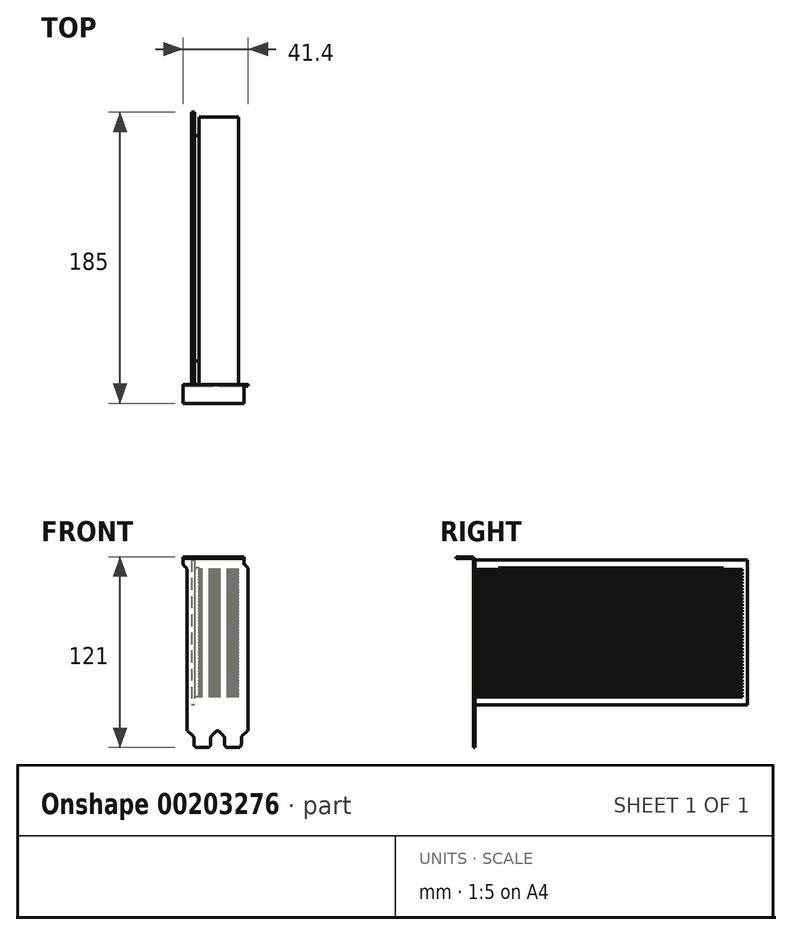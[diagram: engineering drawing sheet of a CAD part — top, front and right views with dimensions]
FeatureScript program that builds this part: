
annotation { "Feature Type Name" : "Feature", "Feature Type Description" : "" }
export const myFeature = defineFeature(function(context is Context, id is Id, definition is map)
    precondition{}
    {
        {
            var Q0;
            Q0=qCreatedBy(makeId("Front.planeOp"),FACE);
            var sketch = newSketch(context, id + "F0", { "sketchPlane" : qUnion([Q0])});
            skLineSegment(sketch, "E0", {"start": v(10.14, 88.78) * mm, "end": v(10.14, -14.22) * mm});
            skLineSegment(sketch, "E1", {"start": v(10.14, -14.22) * mm, "end": v(14.59, -14.22) * mm});
            skLineSegment(sketch, "E2", {"start": v(14.59, -14.22) * mm, "end": v(14.59, -24.82) * mm});
            skLineSegment(sketch, "E3", {"start": v(14.59, -24.82) * mm, "end": v(25.19, -24.82) * mm});
            skLineSegment(sketch, "E4", {"start": v(25.19, -24.82) * mm, "end": v(25.19, -14.22) * mm});
            skLineSegment(sketch, "E5", {"start": v(25.19, -14.22) * mm, "end": v(29.64, -14.22) * mm});
            skLineSegment(sketch, "E6", {"start": v(29.64, -14.22) * mm, "end": v(29.64, 88.78) * mm, "construction": true});
            skLineSegment(sketch, "E7", {"start": v(29.64, -14.22) * mm, "end": v(34.09, -14.22) * mm});
            skLineSegment(sketch, "E8", {"start": v(34.09, -14.22) * mm, "end": v(34.09, -24.82) * mm});
            skLineSegment(sketch, "E9", {"start": v(34.09, -24.82) * mm, "end": v(44.69, -24.82) * mm});
            skLineSegment(sketch, "E10", {"start": v(44.69, -24.82) * mm, "end": v(44.69, -14.22) * mm});
            skLineSegment(sketch, "E11", {"start": v(44.69, -14.22) * mm, "end": v(49.14, -14.22) * mm});
            skLineSegment(sketch, "E12", {"start": v(49.14, -14.22) * mm, "end": v(49.14, 88.78) * mm});
            skLineSegment(sketch, "E13", {"start": v(10.14, 88.78) * mm, "end": v(7.74, 91.18) * mm});
            skLineSegment(sketch, "E14", {"start": v(7.74, 91.18) * mm, "end": v(7.74, 95.18) * mm});
            skLineSegment(sketch, "E15", {"start": v(7.74, 95.18) * mm, "end": v(7.74, 96.18) * mm});
            skLineSegment(sketch, "E16", {"start": v(7.74, 96.18) * mm, "end": v(46.34, 96.18) * mm});
            skLineSegment(sketch, "E17", {"start": v(46.34, 96.18) * mm, "end": v(46.34, 95.18) * mm});
            skLineSegment(sketch, "E18", {"start": v(46.34, 95.18) * mm, "end": v(46.34, 91.58) * mm});
            skLineSegment(sketch, "E19", {"start": v(46.34, 91.58) * mm, "end": v(49.14, 88.78) * mm});
            skLineSegment(sketch, "E20", {"start": v(7.74, 95.18) * mm, "end": v(46.34, 95.18) * mm});
            skSolve(sketch);
        }
        {
            var Q0;
            Q0=makeQuery(id+"F0.imprint","IMPRINT",FACE,{"disambiguationData":[TD([[makeQuery(id+"F0.imprint","IMPRINT",EDGE,{"derivedFrom":sQuery(id+"F0.wireOp",EDGE,"E0")}),1.0]])]});
            extrude(context, id + "F1", {"entities" : qUnion([Q0]), "depth" : 1 * mm});
        }
        {
            var Q0;
            Q0=makeQuery(id+"F1.opExtrude","SWEPT_EDGE",EDGE,{"disambiguationData":[OSD([sQuery(id+"F0.wireOp",EDGE,"E1"),sQuery(id+"F0.wireOp",EDGE,"E2")])]});
            var Q1;
            Q1=makeQuery(id+"F1.opExtrude","SWEPT_EDGE",EDGE,{"disambiguationData":[OSD([sQuery(id+"F0.wireOp",EDGE,"E4"),sQuery(id+"F0.wireOp",EDGE,"E5")])]});
            var Q2;
            Q2=makeQuery(id+"F1.opExtrude","SWEPT_EDGE",EDGE,{"disambiguationData":[OSD([sQuery(id+"F0.wireOp",EDGE,"E7"),sQuery(id+"F0.wireOp",EDGE,"E8")])]});
            var Q3;
            Q3=makeQuery(id+"F1.opExtrude","SWEPT_EDGE",EDGE,{"disambiguationData":[OSD([sQuery(id+"F0.wireOp",EDGE,"E10"),sQuery(id+"F0.wireOp",EDGE,"E11")])]});
            chamfer(context, id + "F2", {"entities" : qUnion([Q0, Q1, Q2, Q3]), "width" : 4 * mm, "tangentPropagation" : true});
        }
        {
            var Q0;
            Q0=makeQuery(id+"F0.imprint","IMPRINT",FACE,{"disambiguationData":[TD([[makeQuery(id+"F0.imprint","IMPRINT",EDGE,{"derivedFrom":sQuery(id+"F0.wireOp",EDGE,"E15")}),-1.0]])]});
            extrude(context, id + "F3", {"entities" : qUnion([Q0]), "operationType" : NewBodyOperationType.ADD, "depth" : 12 * mm});
        }
        {
            var Q0;
            Q0=makeQuery(id+"F3.opExtrude","CAP_EDGE",EDGE,{"disambiguationData":[OSD([sQuery(id+"F0.wireOp",EDGE,"E16")])],"isStart":true});
            var Q1;
            Q1=makeQuery(id+"F1.opExtrude","SWEPT_EDGE",EDGE,{"disambiguationData":[OSD([sQuery(id+"F0.wireOp",EDGE,"E13"),sQuery(id+"F0.wireOp",EDGE,"E14")])]});
            var Q2;
            Q2=makeQuery(id+"F1.opExtrude","SWEPT_EDGE",EDGE,{"disambiguationData":[OSD([sQuery(id+"F0.wireOp",EDGE,"E12"),sQuery(id+"F0.wireOp",EDGE,"E19")])]});
            var Q3;
            Q3=makeQuery(id+"F1.opExtrude","SWEPT_EDGE",EDGE,{"disambiguationData":[OSD([sQuery(id+"F0.wireOp",EDGE,"E18"),sQuery(id+"F0.wireOp",EDGE,"E19")])]});
            var Q4;
            Q4=makeQuery(id+"F1.opExtrude","SWEPT_EDGE",EDGE,{"disambiguationData":[OSD([sQuery(id+"F0.wireOp",EDGE,"E0"),sQuery(id+"F0.wireOp",EDGE,"E13")])]});
            var Q5;
            Q5=makeQuery(id+"F2.opChamfer","BLEND_EDGE",EDGE,{"blendedFrom":[makeQuery(id+"F1.opExtrude","SWEPT_EDGE",EDGE,{"disambiguationData":[OSD([sQuery(id+"F0.wireOp",EDGE,"E1"),sQuery(id+"F0.wireOp",EDGE,"E2")])]}),makeQuery(id+"F1.opExtrude","SWEPT_FACE",FACE,{"disambiguationData":[OSD([sQuery(id+"F0.wireOp",EDGE,"E0")])]})],"blendedInto":[makeQuery(id+"F1.opExtrude","SWEPT_FACE",FACE,{"disambiguationData":[OSD([sQuery(id+"F0.wireOp",EDGE,"E0")])]})]});
            var Q6;
            {var subQ0=sQuery(id+"F0.wireOp",EDGE,"E2");Q6=makeQuery(id+"F2.opChamfer","BLEND_EDGE",EDGE,{"blendedFrom":[makeQuery(id+"F1.opExtrude","SWEPT_EDGE",EDGE,{"disambiguationData":[OSD([sQuery(id+"F0.wireOp",EDGE,"E1"),subQ0])]}),makeQuery(id+"F1.opExtrude","SWEPT_FACE",FACE,{"disambiguationData":[OSD([subQ0])]})],"blendedInto":[makeQuery(id+"F1.opExtrude","SWEPT_FACE",FACE,{"disambiguationData":[OSD([subQ0])]})]});}
            var Q7;
            Q7=makeQuery(id+"F1.opExtrude","SWEPT_EDGE",EDGE,{"disambiguationData":[OSD([sQuery(id+"F0.wireOp",EDGE,"E2"),sQuery(id+"F0.wireOp",EDGE,"E3")])]});
            var Q8;
            Q8=makeQuery(id+"F1.opExtrude","SWEPT_EDGE",EDGE,{"disambiguationData":[OSD([sQuery(id+"F0.wireOp",EDGE,"E3"),sQuery(id+"F0.wireOp",EDGE,"E4")])]});
            var Q9;
            {var subQ0=sQuery(id+"F0.wireOp",EDGE,"E4");Q9=makeQuery(id+"F2.opChamfer","BLEND_EDGE",EDGE,{"blendedFrom":[makeQuery(id+"F1.opExtrude","SWEPT_EDGE",EDGE,{"disambiguationData":[OSD([subQ0,sQuery(id+"F0.wireOp",EDGE,"E5")])]}),makeQuery(id+"F1.opExtrude","SWEPT_FACE",FACE,{"disambiguationData":[OSD([subQ0])]})],"blendedInto":[makeQuery(id+"F1.opExtrude","SWEPT_FACE",FACE,{"disambiguationData":[OSD([subQ0])]})]});}
            var Q10;
            {var subQ0=sQuery(id+"F0.wireOp",EDGE,"E5");Q10=makeQuery(id+"F2.opChamfer","BLEND_EDGE",EDGE,{"blendedFrom":[makeQuery(id+"F1.opExtrude","SWEPT_EDGE",EDGE,{"disambiguationData":[OSD([sQuery(id+"F0.wireOp",EDGE,"E4"),subQ0])]}),makeQuery(id+"F1.opExtrude","SWEPT_FACE",FACE,{"disambiguationData":[OSD([subQ0,sQuery(id+"F0.wireOp",EDGE,"E7")])]})],"blendedInto":[makeQuery(id+"F1.opExtrude","SWEPT_FACE",FACE,{"disambiguationData":[OSD([subQ0,sQuery(id+"F0.wireOp",EDGE,"E7")])]})]});}
            var Q11;
            {var subQ0=sQuery(id+"F0.wireOp",EDGE,"E7");Q11=makeQuery(id+"F2.opChamfer","BLEND_EDGE",EDGE,{"blendedFrom":[makeQuery(id+"F1.opExtrude","SWEPT_EDGE",EDGE,{"disambiguationData":[OSD([subQ0,sQuery(id+"F0.wireOp",EDGE,"E8")])]}),makeQuery(id+"F1.opExtrude","SWEPT_FACE",FACE,{"disambiguationData":[OSD([sQuery(id+"F0.wireOp",EDGE,"E5"),subQ0])]})],"blendedInto":[makeQuery(id+"F1.opExtrude","SWEPT_FACE",FACE,{"disambiguationData":[OSD([sQuery(id+"F0.wireOp",EDGE,"E5"),subQ0])]})]});}
            var Q12;
            {var subQ0=sQuery(id+"F0.wireOp",EDGE,"E8");Q12=makeQuery(id+"F2.opChamfer","BLEND_EDGE",EDGE,{"blendedFrom":[makeQuery(id+"F1.opExtrude","SWEPT_EDGE",EDGE,{"disambiguationData":[OSD([sQuery(id+"F0.wireOp",EDGE,"E7"),subQ0])]}),makeQuery(id+"F1.opExtrude","SWEPT_FACE",FACE,{"disambiguationData":[OSD([subQ0])]})],"blendedInto":[makeQuery(id+"F1.opExtrude","SWEPT_FACE",FACE,{"disambiguationData":[OSD([subQ0])]})]});}
            var Q13;
            Q13=makeQuery(id+"F1.opExtrude","SWEPT_EDGE",EDGE,{"disambiguationData":[OSD([sQuery(id+"F0.wireOp",EDGE,"E8"),sQuery(id+"F0.wireOp",EDGE,"E9")])]});
            var Q14;
            Q14=makeQuery(id+"F1.opExtrude","SWEPT_EDGE",EDGE,{"disambiguationData":[OSD([sQuery(id+"F0.wireOp",EDGE,"E9"),sQuery(id+"F0.wireOp",EDGE,"E10")])]});
            var Q15;
            {var subQ0=sQuery(id+"F0.wireOp",EDGE,"E10");Q15=makeQuery(id+"F2.opChamfer","BLEND_EDGE",EDGE,{"blendedFrom":[makeQuery(id+"F1.opExtrude","SWEPT_EDGE",EDGE,{"disambiguationData":[OSD([subQ0,sQuery(id+"F0.wireOp",EDGE,"E11")])]}),makeQuery(id+"F1.opExtrude","SWEPT_FACE",FACE,{"disambiguationData":[OSD([subQ0])]})],"blendedInto":[makeQuery(id+"F1.opExtrude","SWEPT_FACE",FACE,{"disambiguationData":[OSD([subQ0])]})]});}
            var Q16;
            Q16=makeQuery(id+"F2.opChamfer","BLEND_EDGE",EDGE,{"blendedFrom":[makeQuery(id+"F1.opExtrude","SWEPT_EDGE",EDGE,{"disambiguationData":[OSD([sQuery(id+"F0.wireOp",EDGE,"E10"),sQuery(id+"F0.wireOp",EDGE,"E11")])]}),makeQuery(id+"F1.opExtrude","SWEPT_FACE",FACE,{"disambiguationData":[OSD([sQuery(id+"F0.wireOp",EDGE,"E12")])]})],"blendedInto":[makeQuery(id+"F1.opExtrude","SWEPT_FACE",FACE,{"disambiguationData":[OSD([sQuery(id+"F0.wireOp",EDGE,"E12")])]})]});
            fillet(context, id + "F4", {"entities" : qUnion([Q0, Q1, Q2, Q3, Q4, Q5, Q6, Q7, Q8, Q9, Q10, Q11, Q12, Q13, Q14, Q15, Q16]), "radius" : 2 * mm, "tangentPropagation" : true, "allowEdgeOverflow" : false});
        }
        {
            var Q0;
            {var subQ0=sQuery(id+"F0.wireOp",EDGE,"E20");Q0=makeQuery(id+"F3.boolean.opBoolean","MERGE",FACE,{"derivedFrom":[makeQuery(id+"F1.opExtrude","CAP_FACE",FACE,{"disambiguationData":[OSD([sQuery(id+"F0.wireOp",EDGE,"E0"),sQuery(id+"F0.wireOp",EDGE,"E1"),sQuery(id+"F0.wireOp",EDGE,"E2"),sQuery(id+"F0.wireOp",EDGE,"E3"),sQuery(id+"F0.wireOp",EDGE,"E4"),sQuery(id+"F0.wireOp",EDGE,"E5"),sQuery(id+"F0.wireOp",EDGE,"E7"),sQuery(id+"F0.wireOp",EDGE,"E8"),sQuery(id+"F0.wireOp",EDGE,"E9"),sQuery(id+"F0.wireOp",EDGE,"E10"),sQuery(id+"F0.wireOp",EDGE,"E11"),sQuery(id+"F0.wireOp",EDGE,"E12"),sQuery(id+"F0.wireOp",EDGE,"E13"),sQuery(id+"F0.wireOp",EDGE,"E14"),sQuery(id+"F0.wireOp",EDGE,"E18"),sQuery(id+"F0.wireOp",EDGE,"E19"),subQ0])],"isStart":true}),makeQuery(id+"F3.opExtrude","CAP_FACE",FACE,{"disambiguationData":[OSD([sQuery(id+"F0.wireOp",EDGE,"E15"),sQuery(id+"F0.wireOp",EDGE,"E16"),sQuery(id+"F0.wireOp",EDGE,"E17"),subQ0])],"isStart":true})]});}
            var sketch = newSketch(context, id + "F5", { "sketchPlane" : qUnion([Q0])});
            skLineSegment(sketch, "E21.bottom", {"start": v(-14.94, 100.18) * mm, "end": v(-13.14, 100.18) * mm});
            skLineSegment(sketch, "E21.top", {"start": v(-14.94, 2.18) * mm, "end": v(-13.14, 2.18) * mm});
            skLineSegment(sketch, "E21.left", {"start": v(-14.94, 100.18) * mm, "end": v(-14.94, 2.18) * mm});
            skLineSegment(sketch, "E21.right", {"start": v(-13.14, 100.18) * mm, "end": v(-13.14, 2.18) * mm});
            skLineSegment(sketch, "E22", {"start": v(-19.89, -24.82) * mm, "end": v(-2.6, -24.82) * mm, "construction": true});
            skSolve(sketch);
        }
        {
            var Q0;
            {var subQ0=sQuery(id+"F5.wireOp",EDGE,"E21.top");Q0=makeQuery(id+"F5.imprint","IMPRINT",FACE,{"disambiguationData":[TD([[makeQuery(id+"F5.imprint","IMPRINT",EDGE,{"derivedFrom":subQ0}),1.0]])]});}
            extrude(context, id + "F6", {"entities" : qUnion([Q0]), "operationType" : NewBodyOperationType.ADD, "depth" : 173 * mm});
        }
        {
            var Q0;
            Q0=makeQuery(id+"F6.opExtrude","SWEPT_FACE",FACE,{"disambiguationData":[OSD([sQuery(id+"F5.wireOp",EDGE,"E21.left")])]});
            var sketch = newSketch(context, id + "F7", { "sketchPlane" : qUnion([Q0])});
            skLineSegment(sketch, "E23.bottom", {"start": v(15, 89.18) * mm, "end": v(158, 89.18) * mm});
            skLineSegment(sketch, "E23.top", {"start": v(15, 7.18) * mm, "end": v(158, 7.18) * mm});
            skLineSegment(sketch, "E23.left", {"start": v(15, 89.18) * mm, "end": v(15, 7.18) * mm});
            skLineSegment(sketch, "E23.right", {"start": v(158, 89.18) * mm, "end": v(158, 7.18) * mm});
            skSolve(sketch);
        }
        {
            var Q0;
            Q0=makeQuery(id+"F7.imprint","IMPRINT",FACE,{"disambiguationData":[TD([[makeQuery(id+"F7.imprint","IMPRINT",EDGE,{"derivedFrom":sQuery(id+"F7.wireOp",EDGE,"E23.bottom")}),-1.0]])]});
            extrude(context, id + "F8", {"entities" : qUnion([Q0]), "operationType" : NewBodyOperationType.ADD, "depth" : 3 * mm});
        }
        {
            var Q0;
            Q0=makeQuery(id+"F8.opExtrude","CAP_FACE",FACE,{"disambiguationData":[OSD([sQuery(id+"F7.wireOp",EDGE,"E23.bottom"),sQuery(id+"F7.wireOp",EDGE,"E23.top"),sQuery(id+"F7.wireOp",EDGE,"E23.left"),sQuery(id+"F7.wireOp",EDGE,"E23.right")])],"isStart":false});
            var sketch = newSketch(context, id + "F9", { "sketchPlane" : qUnion([Q0])});
            skLineSegment(sketch, "E24.bottom", {"start": v(0, 7.18) * mm, "end": v(170, 7.18) * mm});
            skLineSegment(sketch, "E24.top", {"start": v(0, 8.18) * mm, "end": v(170, 8.18) * mm});
            skLineSegment(sketch, "E24.left", {"start": v(0, 7.18) * mm, "end": v(0, 8.18) * mm});
            skLineSegment(sketch, "E24.right", {"start": v(170, 7.18) * mm, "end": v(170, 8.18) * mm});
            skLineSegment(sketch, "E25.0.1.0", {"start": v(0, 10.18) * mm, "end": v(170, 10.18) * mm});
            skLineSegment(sketch, "E25.0.1.1", {"start": v(0, 9.18) * mm, "end": v(170, 9.18) * mm});
            skLineSegment(sketch, "E25.0.1.2", {"start": v(0, 9.18) * mm, "end": v(0, 10.18) * mm});
            skLineSegment(sketch, "E25.0.1.3", {"start": v(170, 9.18) * mm, "end": v(170, 10.18) * mm});
            skLineSegment(sketch, "E25.0.2.0", {"start": v(0, 12.18) * mm, "end": v(170, 12.18) * mm});
            skLineSegment(sketch, "E25.0.2.1", {"start": v(0, 11.18) * mm, "end": v(170, 11.18) * mm});
            skLineSegment(sketch, "E25.0.2.2", {"start": v(0, 11.18) * mm, "end": v(0, 12.18) * mm});
            skLineSegment(sketch, "E25.0.2.3", {"start": v(170, 11.18) * mm, "end": v(170, 12.18) * mm});
            skLineSegment(sketch, "E25.0.3.0", {"start": v(0, 14.18) * mm, "end": v(170, 14.18) * mm});
            skLineSegment(sketch, "E25.0.3.1", {"start": v(0, 13.18) * mm, "end": v(170, 13.18) * mm});
            skLineSegment(sketch, "E25.0.3.2", {"start": v(0, 13.18) * mm, "end": v(0, 14.18) * mm});
            skLineSegment(sketch, "E25.0.3.3", {"start": v(170, 13.18) * mm, "end": v(170, 14.18) * mm});
            skLineSegment(sketch, "E25.0.4.0", {"start": v(0, 16.18) * mm, "end": v(170, 16.18) * mm});
            skLineSegment(sketch, "E25.0.4.1", {"start": v(0, 15.18) * mm, "end": v(170, 15.18) * mm});
            skLineSegment(sketch, "E25.0.4.2", {"start": v(0, 15.18) * mm, "end": v(0, 16.18) * mm});
            skLineSegment(sketch, "E25.0.4.3", {"start": v(170, 15.18) * mm, "end": v(170, 16.18) * mm});
            skLineSegment(sketch, "E25.0.5.0", {"start": v(0, 18.18) * mm, "end": v(170, 18.18) * mm});
            skLineSegment(sketch, "E25.0.5.1", {"start": v(0, 17.18) * mm, "end": v(170, 17.18) * mm});
            skLineSegment(sketch, "E25.0.5.2", {"start": v(0, 17.18) * mm, "end": v(0, 18.18) * mm});
            skLineSegment(sketch, "E25.0.5.3", {"start": v(170, 17.18) * mm, "end": v(170, 18.18) * mm});
            skLineSegment(sketch, "E25.0.6.0", {"start": v(0, 20.18) * mm, "end": v(170, 20.18) * mm});
            skLineSegment(sketch, "E25.0.6.1", {"start": v(0, 19.18) * mm, "end": v(170, 19.18) * mm});
            skLineSegment(sketch, "E25.0.6.2", {"start": v(0, 19.18) * mm, "end": v(0, 20.18) * mm});
            skLineSegment(sketch, "E25.0.6.3", {"start": v(170, 19.18) * mm, "end": v(170, 20.18) * mm});
            skLineSegment(sketch, "E25.0.7.0", {"start": v(0, 22.18) * mm, "end": v(170, 22.18) * mm});
            skLineSegment(sketch, "E25.0.7.1", {"start": v(0, 21.18) * mm, "end": v(170, 21.18) * mm});
            skLineSegment(sketch, "E25.0.7.2", {"start": v(0, 21.18) * mm, "end": v(0, 22.18) * mm});
            skLineSegment(sketch, "E25.0.7.3", {"start": v(170, 21.18) * mm, "end": v(170, 22.18) * mm});
            skLineSegment(sketch, "E25.0.8.0", {"start": v(0, 24.18) * mm, "end": v(170, 24.18) * mm});
            skLineSegment(sketch, "E25.0.8.1", {"start": v(0, 23.18) * mm, "end": v(170, 23.18) * mm});
            skLineSegment(sketch, "E25.0.8.2", {"start": v(0, 23.18) * mm, "end": v(0, 24.18) * mm});
            skLineSegment(sketch, "E25.0.8.3", {"start": v(170, 23.18) * mm, "end": v(170, 24.18) * mm});
            skLineSegment(sketch, "E25.0.9.0", {"start": v(0, 26.18) * mm, "end": v(170, 26.18) * mm});
            skLineSegment(sketch, "E25.0.9.1", {"start": v(0, 25.18) * mm, "end": v(170, 25.18) * mm});
            skLineSegment(sketch, "E25.0.9.2", {"start": v(0, 25.18) * mm, "end": v(0, 26.18) * mm});
            skLineSegment(sketch, "E25.0.9.3", {"start": v(170, 25.18) * mm, "end": v(170, 26.18) * mm});
            skLineSegment(sketch, "E25.0.10.0", {"start": v(0, 28.18) * mm, "end": v(170, 28.18) * mm});
            skLineSegment(sketch, "E25.0.10.1", {"start": v(0, 27.18) * mm, "end": v(170, 27.18) * mm});
            skLineSegment(sketch, "E25.0.10.2", {"start": v(0, 27.18) * mm, "end": v(0, 28.18) * mm});
            skLineSegment(sketch, "E25.0.10.3", {"start": v(170, 27.18) * mm, "end": v(170, 28.18) * mm});
            skLineSegment(sketch, "E25.0.11.0", {"start": v(0, 30.18) * mm, "end": v(170, 30.18) * mm});
            skLineSegment(sketch, "E25.0.11.1", {"start": v(0, 29.18) * mm, "end": v(170, 29.18) * mm});
            skLineSegment(sketch, "E25.0.11.2", {"start": v(0, 29.18) * mm, "end": v(0, 30.18) * mm});
            skLineSegment(sketch, "E25.0.11.3", {"start": v(170, 29.18) * mm, "end": v(170, 30.18) * mm});
            skLineSegment(sketch, "E25.0.12.0", {"start": v(0, 32.18) * mm, "end": v(170, 32.18) * mm});
            skLineSegment(sketch, "E25.0.12.1", {"start": v(0, 31.18) * mm, "end": v(170, 31.18) * mm});
            skLineSegment(sketch, "E25.0.12.2", {"start": v(0, 31.18) * mm, "end": v(0, 32.18) * mm});
            skLineSegment(sketch, "E25.0.12.3", {"start": v(170, 31.18) * mm, "end": v(170, 32.18) * mm});
            skLineSegment(sketch, "E25.0.13.0", {"start": v(0, 34.18) * mm, "end": v(170, 34.18) * mm});
            skLineSegment(sketch, "E25.0.13.1", {"start": v(0, 33.18) * mm, "end": v(170, 33.18) * mm});
            skLineSegment(sketch, "E25.0.13.2", {"start": v(0, 33.18) * mm, "end": v(0, 34.18) * mm});
            skLineSegment(sketch, "E25.0.13.3", {"start": v(170, 33.18) * mm, "end": v(170, 34.18) * mm});
            skLineSegment(sketch, "E25.0.14.0", {"start": v(0, 36.18) * mm, "end": v(170, 36.18) * mm});
            skLineSegment(sketch, "E25.0.14.1", {"start": v(0, 35.18) * mm, "end": v(170, 35.18) * mm});
            skLineSegment(sketch, "E25.0.14.2", {"start": v(0, 35.18) * mm, "end": v(0, 36.18) * mm});
            skLineSegment(sketch, "E25.0.14.3", {"start": v(170, 35.18) * mm, "end": v(170, 36.18) * mm});
            skLineSegment(sketch, "E25.0.15.0", {"start": v(0, 38.18) * mm, "end": v(170, 38.18) * mm});
            skLineSegment(sketch, "E25.0.15.1", {"start": v(0, 37.18) * mm, "end": v(170, 37.18) * mm});
            skLineSegment(sketch, "E25.0.15.2", {"start": v(0, 37.18) * mm, "end": v(0, 38.18) * mm});
            skLineSegment(sketch, "E25.0.15.3", {"start": v(170, 37.18) * mm, "end": v(170, 38.18) * mm});
            skLineSegment(sketch, "E25.0.16.0", {"start": v(0, 40.18) * mm, "end": v(170, 40.18) * mm});
            skLineSegment(sketch, "E25.0.16.1", {"start": v(0, 39.18) * mm, "end": v(170, 39.18) * mm});
            skLineSegment(sketch, "E25.0.16.2", {"start": v(0, 39.18) * mm, "end": v(0, 40.18) * mm});
            skLineSegment(sketch, "E25.0.16.3", {"start": v(170, 39.18) * mm, "end": v(170, 40.18) * mm});
            skLineSegment(sketch, "E25.0.17.0", {"start": v(0, 42.18) * mm, "end": v(170, 42.18) * mm});
            skLineSegment(sketch, "E25.0.17.1", {"start": v(0, 41.18) * mm, "end": v(170, 41.18) * mm});
            skLineSegment(sketch, "E25.0.17.2", {"start": v(0, 41.18) * mm, "end": v(0, 42.18) * mm});
            skLineSegment(sketch, "E25.0.17.3", {"start": v(170, 41.18) * mm, "end": v(170, 42.18) * mm});
            skLineSegment(sketch, "E25.0.18.0", {"start": v(0, 44.18) * mm, "end": v(170, 44.18) * mm});
            skLineSegment(sketch, "E25.0.18.1", {"start": v(0, 43.18) * mm, "end": v(170, 43.18) * mm});
            skLineSegment(sketch, "E25.0.18.2", {"start": v(0, 43.18) * mm, "end": v(0, 44.18) * mm});
            skLineSegment(sketch, "E25.0.18.3", {"start": v(170, 43.18) * mm, "end": v(170, 44.18) * mm});
            skLineSegment(sketch, "E25.0.19.0", {"start": v(0, 46.18) * mm, "end": v(170, 46.18) * mm});
            skLineSegment(sketch, "E25.0.19.1", {"start": v(0, 45.18) * mm, "end": v(170, 45.18) * mm});
            skLineSegment(sketch, "E25.0.19.2", {"start": v(0, 45.18) * mm, "end": v(0, 46.18) * mm});
            skLineSegment(sketch, "E25.0.19.3", {"start": v(170, 45.18) * mm, "end": v(170, 46.18) * mm});
            skLineSegment(sketch, "E25.0.20.0", {"start": v(0, 48.18) * mm, "end": v(170, 48.18) * mm});
            skLineSegment(sketch, "E25.0.20.1", {"start": v(0, 47.18) * mm, "end": v(170, 47.18) * mm});
            skLineSegment(sketch, "E25.0.20.2", {"start": v(0, 47.18) * mm, "end": v(0, 48.18) * mm});
            skLineSegment(sketch, "E25.0.20.3", {"start": v(170, 47.18) * mm, "end": v(170, 48.18) * mm});
            skLineSegment(sketch, "E25.0.21.0", {"start": v(0, 50.18) * mm, "end": v(170, 50.18) * mm});
            skLineSegment(sketch, "E25.0.21.1", {"start": v(0, 49.18) * mm, "end": v(170, 49.18) * mm});
            skLineSegment(sketch, "E25.0.21.2", {"start": v(0, 49.18) * mm, "end": v(0, 50.18) * mm});
            skLineSegment(sketch, "E25.0.21.3", {"start": v(170, 49.18) * mm, "end": v(170, 50.18) * mm});
            skLineSegment(sketch, "E25.0.22.0", {"start": v(0, 52.18) * mm, "end": v(170, 52.18) * mm});
            skLineSegment(sketch, "E25.0.22.1", {"start": v(0, 51.18) * mm, "end": v(170, 51.18) * mm});
            skLineSegment(sketch, "E25.0.22.2", {"start": v(0, 51.18) * mm, "end": v(0, 52.18) * mm});
            skLineSegment(sketch, "E25.0.22.3", {"start": v(170, 51.18) * mm, "end": v(170, 52.18) * mm});
            skLineSegment(sketch, "E25.0.23.0", {"start": v(0, 54.18) * mm, "end": v(170, 54.18) * mm});
            skLineSegment(sketch, "E25.0.23.1", {"start": v(0, 53.18) * mm, "end": v(170, 53.18) * mm});
            skLineSegment(sketch, "E25.0.23.2", {"start": v(0, 53.18) * mm, "end": v(0, 54.18) * mm});
            skLineSegment(sketch, "E25.0.23.3", {"start": v(170, 53.18) * mm, "end": v(170, 54.18) * mm});
            skLineSegment(sketch, "E25.0.24.0", {"start": v(0, 56.18) * mm, "end": v(170, 56.18) * mm});
            skLineSegment(sketch, "E25.0.24.1", {"start": v(0, 55.18) * mm, "end": v(170, 55.18) * mm});
            skLineSegment(sketch, "E25.0.24.2", {"start": v(0, 55.18) * mm, "end": v(0, 56.18) * mm});
            skLineSegment(sketch, "E25.0.24.3", {"start": v(170, 55.18) * mm, "end": v(170, 56.18) * mm});
            skLineSegment(sketch, "E25.0.25.0", {"start": v(0, 58.18) * mm, "end": v(170, 58.18) * mm});
            skLineSegment(sketch, "E25.0.25.1", {"start": v(0, 57.18) * mm, "end": v(170, 57.18) * mm});
            skLineSegment(sketch, "E25.0.25.2", {"start": v(0, 57.18) * mm, "end": v(0, 58.18) * mm});
            skLineSegment(sketch, "E25.0.25.3", {"start": v(170, 57.18) * mm, "end": v(170, 58.18) * mm});
            skLineSegment(sketch, "E25.0.26.0", {"start": v(0, 60.18) * mm, "end": v(170, 60.18) * mm});
            skLineSegment(sketch, "E25.0.26.1", {"start": v(0, 59.18) * mm, "end": v(170, 59.18) * mm});
            skLineSegment(sketch, "E25.0.26.2", {"start": v(0, 59.18) * mm, "end": v(0, 60.18) * mm});
            skLineSegment(sketch, "E25.0.26.3", {"start": v(170, 59.18) * mm, "end": v(170, 60.18) * mm});
            skLineSegment(sketch, "E25.0.27.0", {"start": v(0, 62.18) * mm, "end": v(170, 62.18) * mm});
            skLineSegment(sketch, "E25.0.27.1", {"start": v(0, 61.18) * mm, "end": v(170, 61.18) * mm});
            skLineSegment(sketch, "E25.0.27.2", {"start": v(0, 61.18) * mm, "end": v(0, 62.18) * mm});
            skLineSegment(sketch, "E25.0.27.3", {"start": v(170, 61.18) * mm, "end": v(170, 62.18) * mm});
            skLineSegment(sketch, "E25.0.28.0", {"start": v(0, 64.18) * mm, "end": v(170, 64.18) * mm});
            skLineSegment(sketch, "E25.0.28.1", {"start": v(0, 63.18) * mm, "end": v(170, 63.18) * mm});
            skLineSegment(sketch, "E25.0.28.2", {"start": v(0, 63.18) * mm, "end": v(0, 64.18) * mm});
            skLineSegment(sketch, "E25.0.28.3", {"start": v(170, 63.18) * mm, "end": v(170, 64.18) * mm});
            skLineSegment(sketch, "E25.0.29.0", {"start": v(0, 66.18) * mm, "end": v(170, 66.18) * mm});
            skLineSegment(sketch, "E25.0.29.1", {"start": v(0, 65.18) * mm, "end": v(170, 65.18) * mm});
            skLineSegment(sketch, "E25.0.29.2", {"start": v(0, 65.18) * mm, "end": v(0, 66.18) * mm});
            skLineSegment(sketch, "E25.0.29.3", {"start": v(170, 65.18) * mm, "end": v(170, 66.18) * mm});
            skLineSegment(sketch, "E25.0.30.0", {"start": v(0, 68.18) * mm, "end": v(170, 68.18) * mm});
            skLineSegment(sketch, "E25.0.30.1", {"start": v(0, 67.18) * mm, "end": v(170, 67.18) * mm});
            skLineSegment(sketch, "E25.0.30.2", {"start": v(0, 67.18) * mm, "end": v(0, 68.18) * mm});
            skLineSegment(sketch, "E25.0.30.3", {"start": v(170, 67.18) * mm, "end": v(170, 68.18) * mm});
            skLineSegment(sketch, "E25.0.31.0", {"start": v(0, 70.18) * mm, "end": v(170, 70.18) * mm});
            skLineSegment(sketch, "E25.0.31.1", {"start": v(0, 69.18) * mm, "end": v(170, 69.18) * mm});
            skLineSegment(sketch, "E25.0.31.2", {"start": v(0, 69.18) * mm, "end": v(0, 70.18) * mm});
            skLineSegment(sketch, "E25.0.31.3", {"start": v(170, 69.18) * mm, "end": v(170, 70.18) * mm});
            skLineSegment(sketch, "E25.0.32.0", {"start": v(0, 72.18) * mm, "end": v(170, 72.18) * mm});
            skLineSegment(sketch, "E25.0.32.1", {"start": v(0, 71.18) * mm, "end": v(170, 71.18) * mm});
            skLineSegment(sketch, "E25.0.32.2", {"start": v(0, 71.18) * mm, "end": v(0, 72.18) * mm});
            skLineSegment(sketch, "E25.0.32.3", {"start": v(170, 71.18) * mm, "end": v(170, 72.18) * mm});
            skLineSegment(sketch, "E25.0.33.0", {"start": v(0, 74.18) * mm, "end": v(170, 74.18) * mm});
            skLineSegment(sketch, "E25.0.33.1", {"start": v(0, 73.18) * mm, "end": v(170, 73.18) * mm});
            skLineSegment(sketch, "E25.0.33.2", {"start": v(0, 73.18) * mm, "end": v(0, 74.18) * mm});
            skLineSegment(sketch, "E25.0.33.3", {"start": v(170, 73.18) * mm, "end": v(170, 74.18) * mm});
            skLineSegment(sketch, "E25.0.34.0", {"start": v(0, 76.18) * mm, "end": v(170, 76.18) * mm});
            skLineSegment(sketch, "E25.0.34.1", {"start": v(0, 75.18) * mm, "end": v(170, 75.18) * mm});
            skLineSegment(sketch, "E25.0.34.2", {"start": v(0, 75.18) * mm, "end": v(0, 76.18) * mm});
            skLineSegment(sketch, "E25.0.34.3", {"start": v(170, 75.18) * mm, "end": v(170, 76.18) * mm});
            skLineSegment(sketch, "E25.0.35.0", {"start": v(0, 78.18) * mm, "end": v(170, 78.18) * mm});
            skLineSegment(sketch, "E25.0.35.1", {"start": v(0, 77.18) * mm, "end": v(170, 77.18) * mm});
            skLineSegment(sketch, "E25.0.35.2", {"start": v(0, 77.18) * mm, "end": v(0, 78.18) * mm});
            skLineSegment(sketch, "E25.0.35.3", {"start": v(170, 77.18) * mm, "end": v(170, 78.18) * mm});
            skLineSegment(sketch, "E25.0.36.0", {"start": v(0, 80.18) * mm, "end": v(170, 80.18) * mm});
            skLineSegment(sketch, "E25.0.36.1", {"start": v(0, 79.18) * mm, "end": v(170, 79.18) * mm});
            skLineSegment(sketch, "E25.0.36.2", {"start": v(0, 79.18) * mm, "end": v(0, 80.18) * mm});
            skLineSegment(sketch, "E25.0.36.3", {"start": v(170, 79.18) * mm, "end": v(170, 80.18) * mm});
            skLineSegment(sketch, "E25.0.37.0", {"start": v(0, 82.18) * mm, "end": v(170, 82.18) * mm});
            skLineSegment(sketch, "E25.0.37.1", {"start": v(0, 81.18) * mm, "end": v(170, 81.18) * mm});
            skLineSegment(sketch, "E25.0.37.2", {"start": v(0, 81.18) * mm, "end": v(0, 82.18) * mm});
            skLineSegment(sketch, "E25.0.37.3", {"start": v(170, 81.18) * mm, "end": v(170, 82.18) * mm});
            skLineSegment(sketch, "E25.0.38.0", {"start": v(0, 84.18) * mm, "end": v(170, 84.18) * mm});
            skLineSegment(sketch, "E25.0.38.1", {"start": v(0, 83.18) * mm, "end": v(170, 83.18) * mm});
            skLineSegment(sketch, "E25.0.38.2", {"start": v(0, 83.18) * mm, "end": v(0, 84.18) * mm});
            skLineSegment(sketch, "E25.0.38.3", {"start": v(170, 83.18) * mm, "end": v(170, 84.18) * mm});
            skLineSegment(sketch, "E25.0.39.0", {"start": v(0, 86.18) * mm, "end": v(170, 86.18) * mm});
            skLineSegment(sketch, "E25.0.39.1", {"start": v(0, 85.18) * mm, "end": v(170, 85.18) * mm});
            skLineSegment(sketch, "E25.0.39.2", {"start": v(0, 85.18) * mm, "end": v(0, 86.18) * mm});
            skLineSegment(sketch, "E25.0.39.3", {"start": v(170, 85.18) * mm, "end": v(170, 86.18) * mm});
            skLineSegment(sketch, "E25.0.40.0", {"start": v(0, 88.18) * mm, "end": v(170, 88.18) * mm});
            skLineSegment(sketch, "E25.0.40.1", {"start": v(0, 87.18) * mm, "end": v(170, 87.18) * mm});
            skLineSegment(sketch, "E25.0.40.2", {"start": v(0, 87.18) * mm, "end": v(0, 88.18) * mm});
            skLineSegment(sketch, "E25.0.40.3", {"start": v(170, 87.18) * mm, "end": v(170, 88.18) * mm});
            skLineSegment(sketch, "E25.direction1", {"start": v(0, 7.18) * mm, "end": v(25, 7.18) * mm, "construction": true});
            skLineSegment(sketch, "E25.direction2", {"start": v(0, 7.18) * mm, "end": v(0, 9.18) * mm, "construction": true});
            skSolve(sketch);
        }
        {
            var Q0;
            Q0 = qSketchRegion(id + "F9", true);
            extrude(context, id + "F10", {"entities" : qUnion([Q0]), "operationType" : NewBodyOperationType.ADD, "depth" : 25 * mm});
        }
    });
